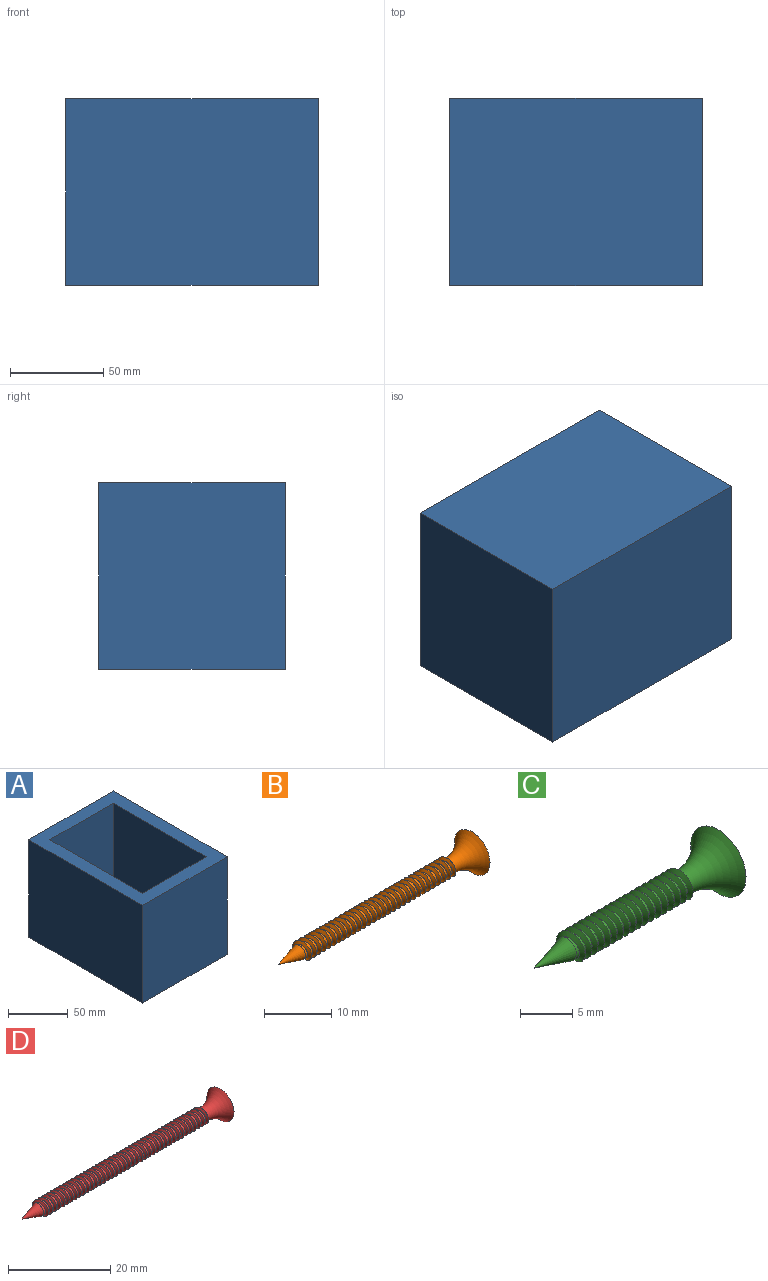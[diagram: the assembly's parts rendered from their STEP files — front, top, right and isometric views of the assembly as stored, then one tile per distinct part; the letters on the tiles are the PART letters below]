
ASSEMBLY  parts=4 mates=3
PART A: 11 faces, bbox 100x135x100 mm
  f0: plane 135x100mm, normal (-1,0,0), area 13500mm2, adj f1,f3,f8,f10
  f1: plane 135x100mm, normal (0,0,-1), area 13500mm2, adj f0,f2,f8,f10
  f2: plane 135x100mm, normal (1,0,0), area 13500mm2, adj f1,f3,f8,f10
  f3: plane 135x100mm, normal (0,0,1), area 5250mm2, adj f0,f2,f4,f6,f7,f8,f9,f10
  f4: plane 110x87.5mm, normal (-1,0,0), area 9625mm2, adj f3,f5,f7,f9
  f5: plane 110x75mm, normal (0,0,1), area 8250mm2, adj f4,f6,f7,f9
  f6: plane 110x87.5mm, normal (1,0,0), area 9625mm2, adj f3,f5,f7,f9
  f7: plane 87.5x75mm, normal (0,-1,0), area 6562.5mm2, adj f3,f4,f5,f6
  f8: plane 100x100mm, normal (0,1,0), area 10000mm2, adj f0,f1,f2,f3
  f9: plane 87.5x75mm, normal (0,1,0), area 6562.5mm2, adj f3,f4,f5,f6
  f10: plane 100x100mm, normal (0,-1,0), area 10000mm2, adj f0,f1,f2,f3
PART B: 54 faces, bbox 42.3x16.2x16.2 mm
  f0: cylinder r=1.25mm len=2.5mm, axis (1,0,0), area 7mm2, adj f1,f36,f51,f52,f53
  f1: cylinder r=1.25mm len=2.5mm, axis (1,0,0), area 3.7mm2, adj f0,f2,f52,f53
  f2: cylinder r=1.25mm len=2.5mm, axis (1,0,0), area 3.7mm2, adj f1,f3,f52,f53
  f3: cylinder r=1.25mm len=2.5mm, axis (1,0,0), area 3.7mm2, adj f2,f4,f52,f53
  f4: cylinder r=1.25mm len=2.5mm, axis (1,0,0), area 3.7mm2, adj f3,f5,f52,f53
  f5: cylinder r=1.25mm len=2.5mm, axis (1,0,0), area 3.7mm2, adj f4,f6,f52,f53
  f6: cylinder r=1.25mm len=2.5mm, axis (1,0,0), area 3.7mm2, adj f5,f7,f52,f53
  f7: cylinder r=1.25mm len=2.5mm, axis (1,0,0), area 3.7mm2, adj f6,f8,f52,f53
  f8: cylinder r=1.25mm len=2.5mm, axis (1,0,0), area 3.7mm2, adj f7,f9,f52,f53
  f9: cylinder r=1.25mm len=2.5mm, axis (1,0,0), area 3.7mm2, adj f8,f10,f52,f53
  f10: cylinder r=1.25mm len=2.5mm, axis (1,0,0), area 3.7mm2, adj f9,f11,f52,f53
  f11: cylinder r=1.25mm len=2.5mm, axis (1,0,0), area 3.7mm2, adj f10,f12,f52,f53
  f12: cylinder r=1.25mm len=2.5mm, axis (1,0,0), area 3.7mm2, adj f11,f13,f52,f53
  f13: cylinder r=1.25mm len=2.5mm, axis (1,0,0), area 3.7mm2, adj f12,f14,f52,f53
  f14: cylinder r=1.25mm len=2.5mm, axis (1,0,0), area 3.7mm2, adj f13,f15,f52,f53
  f15: cylinder r=1.25mm len=2.5mm, axis (1,0,0), area 3.7mm2, adj f14,f16,f52,f53
  f16: cylinder r=1.25mm len=2.5mm, axis (1,0,0), area 3.7mm2, adj f15,f17,f52,f53
  f17: cylinder r=1.25mm len=2.5mm, axis (1,0,0), area 3.7mm2, adj f16,f18,f52,f53
  f18: cylinder r=1.25mm len=2.5mm, axis (1,0,0), area 3.7mm2, adj f17,f19,f52,f53
  f19: cylinder r=1.25mm len=2.5mm, axis (1,0,0), area 3.7mm2, adj f18,f20,f52,f53
  f20: cylinder r=1.25mm len=2.5mm, axis (1,0,0), area 3.7mm2, adj f19,f21,f52,f53
  f21: cylinder r=1.25mm len=2.5mm, axis (1,0,0), area 3.7mm2, adj f20,f22,f52,f53
  f22: cylinder r=1.25mm len=2.5mm, axis (1,0,0), area 3.7mm2, adj f21,f23,f52,f53
  f23: cylinder r=1.25mm len=2.5mm, axis (1,0,0), area 3.7mm2, adj f22,f24,f52,f53
  f24: cylinder r=1.25mm len=2.5mm, axis (1,0,0), area 3.7mm2, adj f23,f25,f52,f53
  f25: cylinder r=1.25mm len=2.5mm, axis (1,0,0), area 3.7mm2, adj f24,f26,f52,f53
  f26: cylinder r=1.25mm len=2.5mm, axis (1,0,0), area 3.7mm2, adj f25,f27,f52,f53
  f27: cylinder r=1.25mm len=2.5mm, axis (1,0,0), area 3.7mm2, adj f26,f28,f52,f53
  f28: cylinder r=1.25mm len=2.5mm, axis (1,0,0), area 3.7mm2, adj f27,f29,f52,f53
  f29: cylinder r=1.25mm len=2.5mm, axis (1,0,0), area 1.7mm2, adj f28,f37,f52,f53
  f30: plane 0.03x0.01mm, normal (0.5,0,-0.87), area 0mm2, adj f34,f39,f44
  f31: plane 0.03x0.01mm, normal (0.5,0,-0.87), area 0mm2, adj f33,f39,f46
  f32: plane 2.45x1.41mm, normal (0.5,0,0.87), area 3.4mm2, adj f33,f34,f35,f39,f47,f48,f49
  f33: plane 2.6x2.45mm, normal (0,1,0), area 1.7mm2, adj f31,f32,f35,f39,f45,f46
  f34: plane 2.6x2.45mm, normal (0,-1,0), area 1.7mm2, adj f30,f32,f35,f39,f42,f44
  f35: plane 7.5x7.5mm, normal (1,0,0), area 36mm2, adj f32,f33,f34,f37,f38,f40,f41,f42
  f36: cone r=0mm half-angle=15.5deg, axis (1,0,0), area 18.3mm2, adj f0
  f37: torus R=7.5mm, axis (1,0,0), area 75.5mm2, adj f29,f35,f50,f52,f53
  f38: plane 2.42x1.4mm, normal (0.5,0,-0.87), area 3.4mm2, adj f35,f40,f41,f43
  f39: plane 1.2x1.2mm, normal (1,0,0), area 1.4mm2, adj f30,f31,f32,f33,f34,f43,f44,f46
  f40: plane 2.42x1.4mm, normal (0,1,0), area 1.7mm2, adj f35,f38,f43
  f41: plane 2.42x1.4mm, normal (0,-1,0), area 1.7mm2, adj f35,f38,f43
  f42: plane 2.43x1.4mm, normal (0,0,1), area 1.7mm2, adj f34,f35,f44
  f43: plane 4x2.45mm, normal (0,0,-1), area 3.4mm2, adj f35,f38,f39,f40,f41,f44,f46
  f44: plane 2.45x1.41mm, normal (0.5,-0.87,0), area 3.4mm2, adj f30,f34,f35,f39,f42,f43
  f45: plane 2.43x1.4mm, normal (0,0,1), area 1.7mm2, adj f33,f35,f46
  f46: plane 2.45x1.41mm, normal (0.5,0.87,0), area 3.4mm2, adj f31,f33,f35,f39,f43,f45
  f47: plane 0.02x0.01mm, normal (0.5,0.87,0), area 0mm2, adj f32,f39,f49
  f48: plane 0.02x0.01mm, normal (0.5,-0.87,0), area 0mm2, adj f32,f39,f49
  f49: plane 1.2x0.02mm, normal (0,0,1), area 0mm2, adj f32,f39,f47,f48
  f50: plane 0.56x0.5mm, normal (0,0,1), area 0.1mm2, adj f37,f52,f53
  f51: plane 0.58x0.5mm, normal (0,0,-1), area 0.1mm2, adj f0,f52,f53
  f52: bspline ~31.79x4.04mm, area 164.4mm2, adj f0,f1,f2,f3,f4,f5,f6,f7
  f53: bspline ~31.79x3.5mm, area 164mm2, adj f0,f1,f2,f3,f4,f5,f6,f7
PART C: 26 faces, bbox 26.3x16.2x16.2 mm
  f0: cylinder r=1.25mm len=15.5mm, axis (1,0,0), area 37.3mm2, adj f7,f8,f21,f22,f24,f25
  f1: plane 0.03x0.01mm, normal (0.5,0,-0.87), area 0mm2, adj f5,f10,f15
  f2: plane 0.03x0.01mm, normal (0.5,0,-0.87), area 0mm2, adj f4,f10,f17
  f3: plane 2.45x1.41mm, normal (0.5,0,0.87), area 3.4mm2, adj f4,f5,f6,f10,f18,f19,f20
  f4: plane 2.6x2.45mm, normal (0,1,0), area 1.7mm2, adj f2,f3,f6,f10,f16,f17
  f5: plane 2.6x2.45mm, normal (0,-1,0), area 1.7mm2, adj f1,f3,f6,f10,f13,f15
  f6: plane 7.5x7.5mm, normal (1,0,0), area 36mm2, adj f3,f4,f5,f8,f9,f11,f12,f13
  f7: cone r=0mm half-angle=15.5deg, axis (1,0,0), area 18.3mm2, adj f0,f23
  f8: torus R=7.5mm, axis (1,0,0), area 75.4mm2, adj f0,f6,f21,f25
  f9: plane 2.42x1.4mm, normal (0.5,0,-0.87), area 3.4mm2, adj f6,f11,f12,f14
  f10: plane 1.2x1.2mm, normal (1,0,0), area 1.4mm2, adj f1,f2,f3,f4,f5,f14,f15,f17
  f11: plane 2.42x1.4mm, normal (0,1,0), area 1.7mm2, adj f6,f9,f14
  f12: plane 2.42x1.4mm, normal (0,-1,0), area 1.7mm2, adj f6,f9,f14
  f13: plane 2.43x1.4mm, normal (0,0,1), area 1.7mm2, adj f5,f6,f15
  f14: plane 4x2.45mm, normal (0,0,-1), area 3.4mm2, adj f6,f9,f10,f11,f12,f15,f17
  f15: plane 2.45x1.41mm, normal (0.5,-0.87,0), area 3.4mm2, adj f1,f5,f6,f10,f13,f14
  f16: plane 2.43x1.4mm, normal (0,0,1), area 1.7mm2, adj f4,f6,f17
  f17: plane 2.45x1.41mm, normal (0.5,0.87,0), area 3.4mm2, adj f2,f4,f6,f10,f14,f16
  f18: plane 0.02x0.01mm, normal (0.5,0.87,0), area 0mm2, adj f3,f10,f20
  f19: plane 0.02x0.01mm, normal (0.5,-0.87,0), area 0mm2, adj f3,f10,f20
  f20: plane 1.2x0.02mm, normal (0,0,1), area 0mm2, adj f3,f10,f18,f19
  f21: plane 0.56x0.5mm, normal (0,0,1), area 0.1mm2, adj f0,f8,f24,f25
  f22: plane 0.58x0.5mm, normal (0,0,-1), area 0.1mm2, adj f0,f23,f24,f25
  f23: cylinder r=1.25mm len=0.32mm, axis (-1,0,0), area 0mm2, adj f7,f22,f24
  f24: bspline ~15.79x4.04mm, area 98.3mm2, adj f0,f21,f22,f23,f25
  f25: bspline ~15.79x4.04mm, area 97.9mm2, adj f0,f8,f21,f22,f24
PART D: 64 faces, bbox 56.6x17.4x17.4 mm
  f0: cylinder r=1.45mm len=2.9mm, axis (1,0,0), area 9.3mm2, adj f1,f45,f61,f62,f63
  f1: cylinder r=1.45mm len=2.9mm, axis (1,0,0), area 5.1mm2, adj f0,f2,f62,f63
  f2: cylinder r=1.45mm len=2.9mm, axis (1,0,0), area 5.1mm2, adj f1,f3,f62,f63
  f3: cylinder r=1.45mm len=2.9mm, axis (1,0,0), area 5.1mm2, adj f2,f4,f62,f63
  f4: cylinder r=1.45mm len=2.9mm, axis (1,0,0), area 5.1mm2, adj f3,f5,f62,f63
  f5: cylinder r=1.45mm len=2.9mm, axis (1,0,0), area 5.1mm2, adj f4,f6,f62,f63
  f6: cylinder r=1.45mm len=2.9mm, axis (1,0,0), area 5.1mm2, adj f5,f7,f62,f63
  f7: cylinder r=1.45mm len=2.9mm, axis (1,0,0), area 5.1mm2, adj f6,f8,f62,f63
  f8: cylinder r=1.45mm len=2.9mm, axis (1,0,0), area 5.1mm2, adj f7,f9,f62,f63
  f9: cylinder r=1.45mm len=2.9mm, axis (1,0,0), area 5.1mm2, adj f8,f10,f62,f63
  f10: cylinder r=1.45mm len=2.9mm, axis (1,0,0), area 5.1mm2, adj f9,f11,f62,f63
  f11: cylinder r=1.45mm len=2.9mm, axis (1,0,0), area 5.1mm2, adj f10,f12,f62,f63
  f12: cylinder r=1.45mm len=2.9mm, axis (1,0,0), area 5.1mm2, adj f11,f13,f62,f63
  f13: cylinder r=1.45mm len=2.9mm, axis (1,0,0), area 5.1mm2, adj f12,f14,f62,f63
  f14: cylinder r=1.45mm len=2.9mm, axis (1,0,0), area 5.1mm2, adj f13,f15,f62,f63
  f15: cylinder r=1.45mm len=2.9mm, axis (1,0,0), area 5.1mm2, adj f14,f16,f62,f63
  f16: cylinder r=1.45mm len=2.9mm, axis (1,0,0), area 5.1mm2, adj f15,f17,f62,f63
  f17: cylinder r=1.45mm len=2.9mm, axis (1,0,0), area 5.1mm2, adj f16,f18,f62,f63
  f18: cylinder r=1.45mm len=2.9mm, axis (1,0,0), area 5.1mm2, adj f17,f19,f62,f63
  f19: cylinder r=1.45mm len=2.9mm, axis (1,0,0), area 5.1mm2, adj f18,f20,f62,f63
  f20: cylinder r=1.45mm len=2.9mm, axis (1,0,0), area 5.1mm2, adj f19,f21,f62,f63
  f21: cylinder r=1.45mm len=2.9mm, axis (1,0,0), area 5.1mm2, adj f20,f22,f62,f63
  f22: cylinder r=1.45mm len=2.9mm, axis (1,0,0), area 5.1mm2, adj f21,f23,f62,f63
  f23: cylinder r=1.45mm len=2.9mm, axis (1,0,0), area 5.1mm2, adj f22,f24,f62,f63
  f24: cylinder r=1.45mm len=2.9mm, axis (1,0,0), area 5.1mm2, adj f23,f25,f62,f63
  f25: cylinder r=1.45mm len=2.9mm, axis (1,0,0), area 5.1mm2, adj f24,f26,f62,f63
  f26: cylinder r=1.45mm len=2.9mm, axis (1,0,0), area 5.1mm2, adj f25,f27,f62,f63
  f27: cylinder r=1.45mm len=2.9mm, axis (1,0,0), area 5.1mm2, adj f26,f28,f62,f63
  f28: cylinder r=1.45mm len=2.9mm, axis (1,0,0), area 5.1mm2, adj f27,f29,f62,f63
  f29: cylinder r=1.45mm len=2.9mm, axis (1,0,0), area 5.1mm2, adj f28,f30,f62,f63
  f30: cylinder r=1.45mm len=2.9mm, axis (1,0,0), area 5.1mm2, adj f29,f31,f62,f63
  f31: cylinder r=1.45mm len=2.9mm, axis (1,0,0), area 5.1mm2, adj f30,f32,f62,f63
  f32: cylinder r=1.45mm len=2.9mm, axis (1,0,0), area 5.1mm2, adj f31,f33,f62,f63
  f33: cylinder r=1.45mm len=2.9mm, axis (1,0,0), area 5.1mm2, adj f32,f34,f62,f63
  f34: cylinder r=1.45mm len=2.9mm, axis (1,0,0), area 5.1mm2, adj f33,f35,f62,f63
  f35: cylinder r=1.45mm len=2.9mm, axis (1,0,0), area 5.1mm2, adj f34,f36,f62,f63
  f36: cylinder r=1.45mm len=2.9mm, axis (1,0,0), area 5.1mm2, adj f35,f37,f62,f63
  f37: cylinder r=1.45mm len=2.9mm, axis (1,0,0), area 5.1mm2, adj f36,f38,f62,f63
  f38: cylinder r=1.45mm len=2.9mm, axis (1,0,0), area 5.1mm2, adj f37,f39,f62,f63
  f39: cylinder r=1.45mm len=2.9mm, axis (1,0,0), area 2.4mm2, adj f38,f46,f62,f63
  f40: plane 7.5x7.5mm, normal (1,0,0), area 36mm2, adj f43,f44,f46,f47,f49,f50,f51,f52
  f41: plane 0.03x0.01mm, normal (0.5,0,-0.87), area 0mm2, adj f44,f48,f54
  f42: plane 0.03x0.01mm, normal (0.5,0,-0.87), area 0mm2, adj f43,f48,f56
  f43: plane 2.6x2.45mm, normal (0,1,0), area 1.7mm2, adj f40,f42,f48,f49,f55,f56
  f44: plane 2.6x2.45mm, normal (0,-1,0), area 1.7mm2, adj f40,f41,f48,f49,f52,f54
  f45: cone r=0mm half-angle=17.9deg, axis (1,0,0), area 21.5mm2, adj f0
  f46: torus R=8.03mm, axis (1,0,0), area 78.3mm2, adj f39,f40,f60,f62,f63
  f47: plane 2.42x1.4mm, normal (0.5,0,-0.87), area 3.4mm2, adj f40,f50,f51,f53
  f48: plane 1.2x1.2mm, normal (1,0,0), area 1.4mm2, adj f41,f42,f43,f44,f49,f53,f54,f56
  f49: plane 2.45x1.41mm, normal (0.5,0,0.87), area 3.4mm2, adj f40,f43,f44,f48,f57,f58,f59
  f50: plane 2.42x1.4mm, normal (0,1,0), area 1.7mm2, adj f40,f47,f53
  f51: plane 2.42x1.4mm, normal (0,-1,0), area 1.7mm2, adj f40,f47,f53
  f52: plane 2.43x1.4mm, normal (0,0,1), area 1.7mm2, adj f40,f44,f54
  f53: plane 4x2.45mm, normal (0,0,-1), area 3.4mm2, adj f40,f47,f48,f50,f51,f54,f56
  f54: plane 2.45x1.41mm, normal (0.5,-0.87,0), area 3.4mm2, adj f40,f41,f44,f48,f52,f53
  f55: plane 2.43x1.4mm, normal (0,0,1), area 1.7mm2, adj f40,f43,f56
  f56: plane 2.45x1.41mm, normal (0.5,0.87,0), area 3.4mm2, adj f40,f42,f43,f48,f53,f55
  f57: plane 0.02x0.01mm, normal (0.5,0.87,0), area 0mm2, adj f48,f49,f59
  f58: plane 0.02x0.01mm, normal (0.5,-0.87,0), area 0mm2, adj f48,f49,f59
  f59: plane 1.2x0.02mm, normal (0,0,1), area 0mm2, adj f48,f49,f57,f58
  f60: plane 0.56x0.5mm, normal (0,0,1), area 0.1mm2, adj f46,f62,f63
  f61: plane 0.58x0.5mm, normal (0,0,-1), area 0.1mm2, adj f0,f62,f63
  f62: bspline ~45.79x4.5mm, area 247.7mm2, adj f0,f1,f2,f3,f4,f5,f6,f7
  f63: bspline ~45.79x3.9mm, area 247.7mm2, adj f0,f1,f2,f3,f4,f5,f6,f7
PLACE A rot(axis=(-0.58,-0.58,-0.58),120deg) t=(66.76,5.47,4.39)mm fixed
PLACE B rot(axis=(-1,0,0),160.4deg) t=(103.81,1.34,66.54)mm
PLACE C rot(axis=(1,0,0),180deg) t=(103.81,5.68,56.29)mm
PLACE D t=(103.81,5.68,80.49)mm
MATE cylindrical C.f8 <-> A.f8  axis (1,0,0) through (79.26,5.68,29.39)mm
MATE cylindrical D.f45 <-> A.f8  axis (1,0,0) through (79.26,5.68,79.39)mm
MATE cylindrical B.f37 <-> A.f8  axis (1,0,0) through (79.26,5.68,54.39)mm
